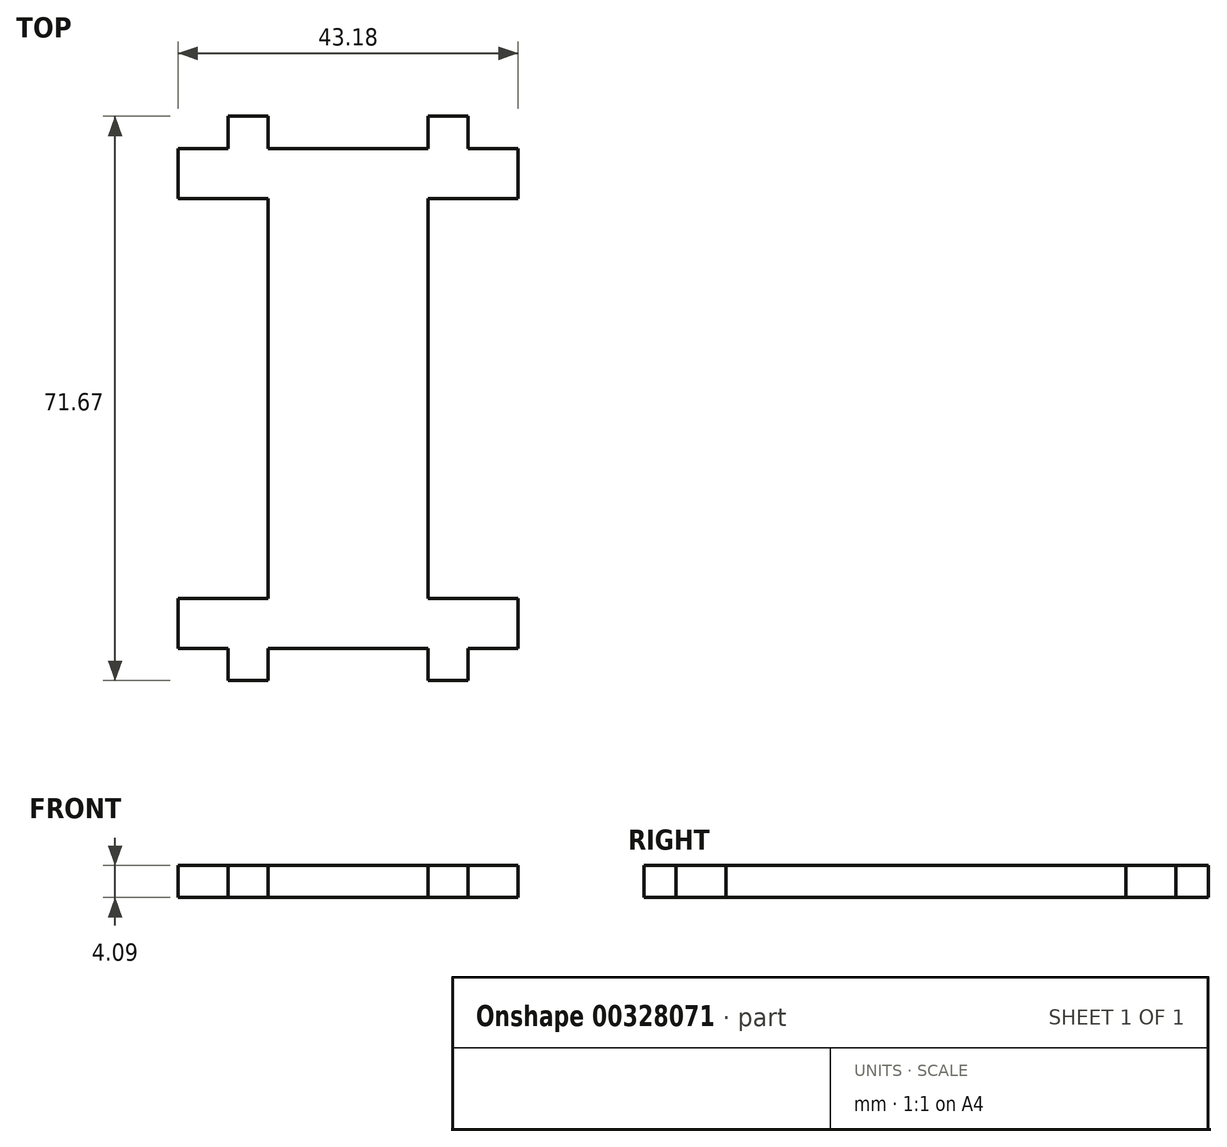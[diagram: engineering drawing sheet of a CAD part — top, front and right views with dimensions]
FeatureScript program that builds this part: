
annotation { "Feature Type Name" : "Feature", "Feature Type Description" : "" }
export const myFeature = defineFeature(function(context is Context, id is Id, definition is map)
    precondition{}
    {
        {
            var Q0;
            Q0=qCreatedBy(makeId("Top.planeOp"),FACE);
            var sketch = newSketch(context, id + "F0", { "sketchPlane" : qUnion([Q0])});
            skLineSegment(sketch, "E0", {"start": v(0, 0) * mm, "end": v(-12.7, 0) * mm, "construction": true});
            skLineSegment(sketch, "E1.MirrorCS", {"start": v(0, 0) * mm, "end": v(12.7, 0) * mm, "construction": true});
            skLineSegment(sketch, "E2.bottom", {"start": v(15.24, -2.04) * mm, "end": v(10.16, -2.04) * mm});
            skLineSegment(sketch, "E2.top", {"start": v(15.24, 2.04) * mm, "end": v(10.16, 2.04) * mm});
            skLineSegment(sketch, "E2.left", {"start": v(15.24, -2.04) * mm, "end": v(15.24, 2.04) * mm});
            skLineSegment(sketch, "E2.right", {"start": v(10.16, -2.04) * mm, "end": v(10.16, 2.04) * mm});
            skPoint(sketch, "E2.middle", {"position": v(12.7, 0) * mm});
            skLineSegment(sketch, "E3.MirrorCS", {"start": v(-15.24, 2.04) * mm, "end": v(-10.16, 2.04) * mm});
            skLineSegment(sketch, "E4.MirrorCS", {"start": v(-10.16, -2.04) * mm, "end": v(-10.16, 2.04) * mm});
            skLineSegment(sketch, "E5.MirrorCS", {"start": v(-15.24, -2.04) * mm, "end": v(-15.24, 2.04) * mm});
            skLineSegment(sketch, "E6.MirrorCS", {"start": v(-15.24, -2.04) * mm, "end": v(-10.16, -2.04) * mm});
            skLineSegment(sketch, "E7", {"start": v(-10.16, -2.04) * mm, "end": v(10.16, -2.04) * mm});
            skLineSegment(sketch, "E8", {"start": v(-15.24, -2.04) * mm, "end": v(-21.6, -2.04) * mm});
            skLineSegment(sketch, "E9.MirrorCS", {"start": v(15.24, -2.04) * mm, "end": v(21.6, -2.04) * mm});
            skLineSegment(sketch, "E10", {"start": v(-21.6, -2.04) * mm, "end": v(-21.6, -8.4) * mm});
            skLineSegment(sketch, "E11.MirrorCS", {"start": v(21.6, -2.04) * mm, "end": v(21.6, -8.4) * mm});
            skLineSegment(sketch, "E12", {"start": v(-21.6, -8.4) * mm, "end": v(21.6, -8.4) * mm});
            skLineSegment(sketch, "E13", {"start": v(0, -8.4) * mm, "end": v(-10.16, -8.4) * mm, "construction": true});
            skLineSegment(sketch, "E14", {"start": v(-10.16, -8.4) * mm, "end": v(-10.16, -59.2) * mm});
            skLineSegment(sketch, "E15.MirrorCS", {"start": v(10.16, -8.4) * mm, "end": v(10.16, -59.2) * mm});
            skLineSegment(sketch, "E16", {"start": v(-10.16, -33.8) * mm, "end": v(10.16, -33.8) * mm, "construction": true});
            skLineSegment(sketch, "E17.MirrorCS", {"start": v(15.24, -65.54) * mm, "end": v(10.16, -65.54) * mm});
            skLineSegment(sketch, "E18.MirrorCS", {"start": v(15.24, -69.63) * mm, "end": v(10.16, -69.63) * mm});
            skLineSegment(sketch, "E19.MirrorCS", {"start": v(15.24, -65.54) * mm, "end": v(15.24, -69.63) * mm});
            skLineSegment(sketch, "E20.MirrorCS", {"start": v(-15.24, -65.54) * mm, "end": v(-10.16, -65.54) * mm});
            skLineSegment(sketch, "E21.MirrorCS", {"start": v(10.16, -65.54) * mm, "end": v(10.16, -69.63) * mm});
            skLineSegment(sketch, "E22.MirrorCS", {"start": v(15.24, -65.54) * mm, "end": v(21.6, -65.54) * mm});
            skLineSegment(sketch, "E23.MirrorCS", {"start": v(-15.24, -65.54) * mm, "end": v(-15.24, -69.63) * mm});
            skLineSegment(sketch, "E24.MirrorCS", {"start": v(-15.24, -69.63) * mm, "end": v(-10.16, -69.63) * mm});
            skLineSegment(sketch, "E25.MirrorCS", {"start": v(-15.24, -65.54) * mm, "end": v(-21.6, -65.54) * mm});
            skLineSegment(sketch, "E26.MirrorCS", {"start": v(-10.16, -65.54) * mm, "end": v(-10.16, -69.63) * mm});
            skLineSegment(sketch, "E27.MirrorCS", {"start": v(-21.6, -65.54) * mm, "end": v(-21.6, -59.2) * mm});
            skPoint(sketch, "E28.MirrorP", {"position": v(12.7, -67.59) * mm});
            skLineSegment(sketch, "E29.MirrorCS", {"start": v(21.6, -65.54) * mm, "end": v(21.6, -59.2) * mm});
            skLineSegment(sketch, "E30.MirrorCS", {"start": v(-21.6, -59.2) * mm, "end": v(21.6, -59.2) * mm});
            skLineSegment(sketch, "E31.MirrorCS", {"start": v(0, -67.59) * mm, "end": v(-12.7, -67.59) * mm, "construction": true});
            skLineSegment(sketch, "E32.MirrorCS", {"start": v(0, -67.59) * mm, "end": v(12.7, -67.59) * mm, "construction": true});
            skLineSegment(sketch, "E33.MirrorCS", {"start": v(0, -59.2) * mm, "end": v(-10.16, -59.2) * mm, "construction": true});
            skLineSegment(sketch, "E34.MirrorCS", {"start": v(-10.16, -65.54) * mm, "end": v(10.16, -65.54) * mm});
            skSolve(sketch);
        }
        {
            var Q0;
            Q0 = qSketchRegion(id + "F0", true);
            extrude(context, id + "F1", {"entities" : qUnion([Q0]), "depth" : 4.1 * mm});
        }
    });
